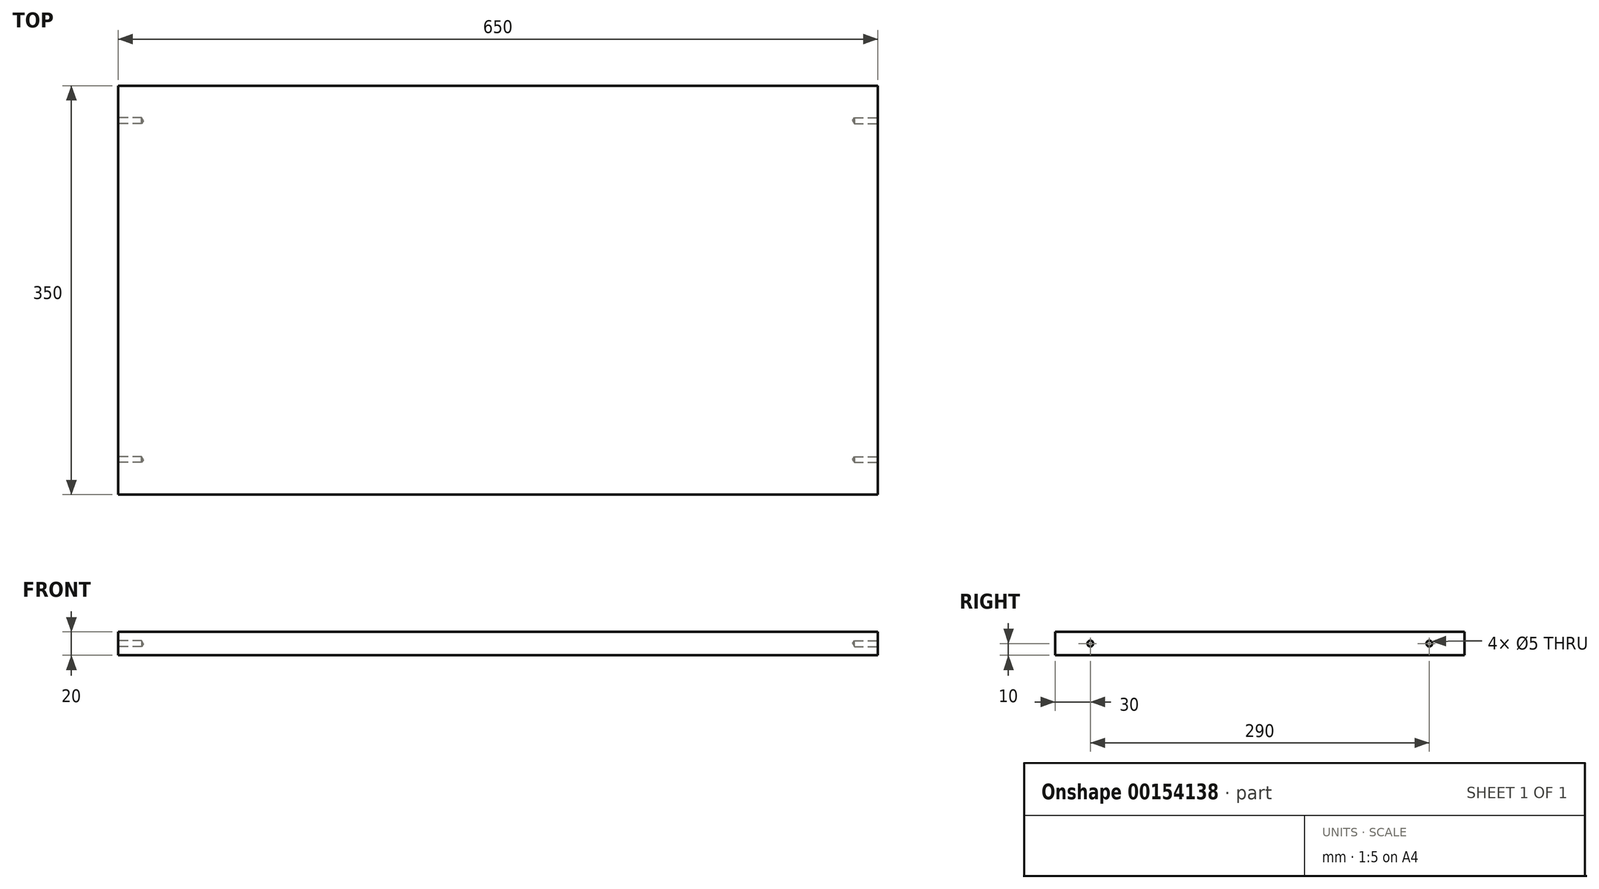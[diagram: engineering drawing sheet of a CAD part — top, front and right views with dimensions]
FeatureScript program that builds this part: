
annotation { "Feature Type Name" : "Feature", "Feature Type Description" : "" }
export const myFeature = defineFeature(function(context is Context, id is Id, definition is map)
    precondition{}
    {
        {
            var Q0;
            Q0=qCreatedBy(makeId("Top.planeOp"),FACE);
            var sketch = newSketch(context, id + "F0", { "sketchPlane" : qUnion([Q0])});
            skLineSegment(sketch, "E0.bottom", {"start": v(325, -175) * mm, "end": v(-325, -175) * mm});
            skLineSegment(sketch, "E0.top", {"start": v(325, 175) * mm, "end": v(-325, 175) * mm});
            skLineSegment(sketch, "E0.left", {"start": v(325, -175) * mm, "end": v(325, 175) * mm});
            skLineSegment(sketch, "E0.right", {"start": v(-325, -175) * mm, "end": v(-325, 175) * mm});
            skPoint(sketch, "E0.middle", {"position": v(0, 0) * mm});
            skSolve(sketch);
        }
        {
            var Q0;
            Q0 = qSketchRegion(id + "F0", true);
            extrude(context, id + "F1", {"entities" : qUnion([Q0]), "depth" : 20 * mm});
        }
        {
            var Q0;
            Q0=makeQuery(id+"F1.opExtrude","SWEPT_FACE",FACE,{"disambiguationData":[OSD([sQuery(id+"F0.wireOp",EDGE,"E0.right")])]});
            var sketch = newSketch(context, id + "F2", { "sketchPlane" : qUnion([Q0])});
            skPoint(sketch, "E1", {"position": v(-145, 10) * mm});
            skPoint(sketch, "E2", {"position": v(145, 10) * mm});
            skSolve(sketch);
        }
        {
            var Q0;
            Q0=makeQuery(id+"F1.opExtrude","SWEPT_FACE",FACE,{"disambiguationData":[OSD([sQuery(id+"F0.wireOp",EDGE,"E0.left")])]});
            var sketch = newSketch(context, id + "F3", { "sketchPlane" : qUnion([Q0])});
            skPoint(sketch, "E3", {"position": v(-145, 10) * mm});
            skPoint(sketch, "E4", {"position": v(145, 10) * mm});
            skSolve(sketch);
        }
        {
            var Q0;
            Q0=sQuery(id+"F2.wireOp",VERTEX,"E1");
            var Q1;
            Q1=sQuery(id+"F2.wireOp",VERTEX,"E2");
            var Q2;
            Q2=sQuery(id+"F3.wireOp",VERTEX,"E3");
            var Q3;
            Q3=sQuery(id+"F3.wireOp",VERTEX,"E4");
            var Q4;
            Q4=makeQuery(id+"F1.opExtrude","SWEPT_BODY",BODY,{"disambiguationData":[OSD([sQuery(id+"F0.wireOp",EDGE,"E0.bottom"),sQuery(id+"F0.wireOp",EDGE,"E0.top"),sQuery(id+"F0.wireOp",EDGE,"E0.left"),sQuery(id+"F0.wireOp",EDGE,"E0.right")])]});
            hole(context, id + "F4", {"style" : HoleStyle.SIMPLE, "endStyle" : HoleEndStyle.BLIND, "standardTappedOrClearance" : lookupTablePath({ "standard" : "ISO", "engagement" : "75%", "pitch" : "1 mm", "size" : "M6", "type" : "Tapped" }), "standardBlindInLast" : lookupTablePath({ "standard" : "ISO", "engagement" : "75%", "pitch" : "1 mm", "size" : "M6", "type" : "Tapped" }), "holeDiameter" : 5 * mm, "holeDepth" : 20 * mm, "locations" : qUnion([Q0, Q1, Q2, Q3]), "scope" : qUnion([Q4]), "majorDiameter" : 6 * mm});
        }
    });
